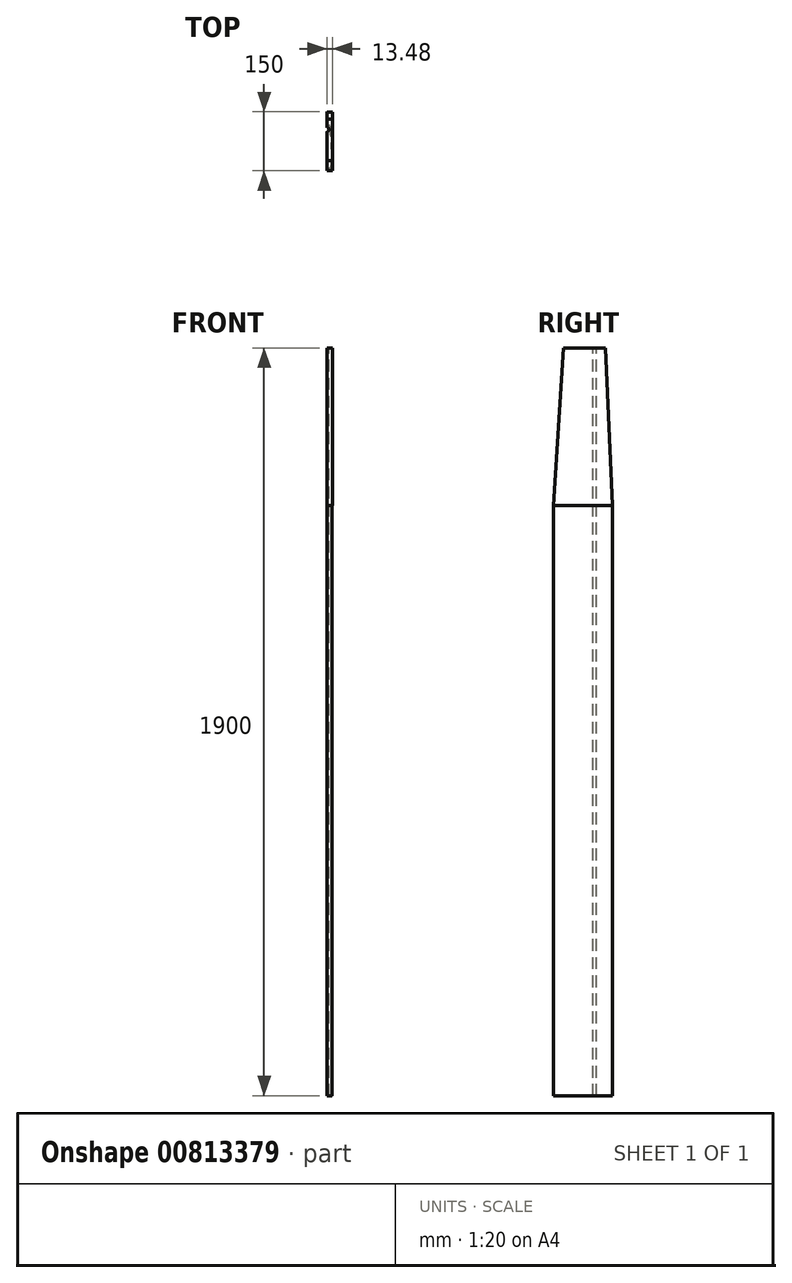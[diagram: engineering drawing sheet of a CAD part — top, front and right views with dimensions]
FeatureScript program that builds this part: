
annotation { "Feature Type Name" : "Feature", "Feature Type Description" : "" }
export const myFeature = defineFeature(function(context is Context, id is Id, definition is map)
    precondition{}
    {
        {
            var Q0;
            Q0=qCreatedBy(makeId("Top.planeOp"),FACE);
            var sketch = newSketch(context, id + "F0", { "sketchPlane" : qUnion([Q0])});
            skFitSpline(sketch, "E0", {"points": [v(0, 0) * mm, v(10.85, 19.16) * mm, v(11.95, 47.27) * mm, v(0, 150) * mm], "startDerivative": vector(86.36, 0) * mm, "endDerivative": vector(-49.91, 214.58) * mm});
            skLineSegment(sketch, "E1", {"start": v(0, 0) * mm, "end": v(0, 150) * mm});
            skSolve(sketch);
        }
        {
            var Q0;
            Q0=makeQuery(id+"F0.imprint","IMPRINT",FACE,{"disambiguationData":[TD([[makeQuery(id+"F0.imprint","IMPRINT",EDGE,{"derivedFrom":sQuery(id+"F0.wireOp",EDGE,"E0")}),1.0]])]});
            extrude(context, id + "F1", {"entities" : qUnion([Q0]), "oppositeDirection" : true, "depth" : 1500 * mm, "offsetDistance" : 25 * mm});
        }
        {
            var Q0;
            Q0=qCreatedBy(makeId("Top.planeOp"),FACE);
            var sketch = newSketch(context, id + "F2", { "sketchPlane" : qUnion([Q0])});
            skLineSegment(sketch, "E2.bottom", {"start": v(0, 0) * mm, "end": v(13.41, 0) * mm});
            skLineSegment(sketch, "E2.top", {"start": v(0, 149.72) * mm, "end": v(13.41, 149.72) * mm});
            skLineSegment(sketch, "E2.left", {"start": v(0, 0) * mm, "end": v(0, 149.72) * mm});
            skLineSegment(sketch, "E2.right", {"start": v(13.41, 0) * mm, "end": v(13.41, 149.72) * mm});
            skSolve(sketch);
        }
        {
            var Q0;
            Q0=qCreatedBy(makeId("Top.planeOp"),FACE);
            cPlane(context, id + "F3", {"entities" : qUnion([Q0]), "cplaneType" : CPlaneType.OFFSET, "offset" : 400 * mm, "width" : 150 * mm, "height" : 150 * mm});
        }
        {
            var Q0;
            Q0=qCreatedBy(id+"F3.planeOp",FACE);
            var sketch = newSketch(context, id + "F4", { "sketchPlane" : qUnion([Q0])});
            skLineSegment(sketch, "E3.bottom", {"start": v(0, 25.55) * mm, "end": v(13.48, 25.55) * mm});
            skLineSegment(sketch, "E3.top", {"start": v(0, 131.68) * mm, "end": v(13.48, 131.68) * mm});
            skLineSegment(sketch, "E3.left", {"start": v(0, 25.55) * mm, "end": v(0, 131.68) * mm});
            skLineSegment(sketch, "E3.right", {"start": v(13.48, 25.55) * mm, "end": v(13.48, 131.68) * mm});
            skSolve(sketch);
        }
        {
            var Q1;
            Q1=makeQuery(id+"F4.imprint","IMPRINT",FACE,{"disambiguationData":[TD([[makeQuery(id+"F4.imprint","IMPRINT",EDGE,{"derivedFrom":sQuery(id+"F4.wireOp",EDGE,"E3.bottom")}),1.0]])]});
            var Q2;
            Q2=makeQuery(id+"F2.imprint","IMPRINT",FACE,{"disambiguationData":[TD([[makeQuery(id+"F2.imprint","IMPRINT",EDGE,{"derivedFrom":sQuery(id+"F2.wireOp",EDGE,"E2.bottom")}),1.0]])]});
            loft(context, id + "F5", {"operationType" : NewBodyOperationType.ADD, "sheetProfilesArray" : [{ "sheetProfileEntities" : qUnion([Q1]) }, { "sheetProfileEntities" : qUnion([Q2]) }]});
        }
        {
            var Q0;
            Q0=qCreatedBy(id+"F3.planeOp",FACE);
            var sketch = newSketch(context, id + "F6", { "sketchPlane" : qUnion([Q0])});
            skArc(sketch, "E4", {"start": v(0, 100) * mm, "mid": v(5, 105) * mm, "end": v(0, 110) * mm});
            skLineSegment(sketch, "E5", {"start": v(0, 100) * mm, "end": v(0, 110) * mm});
            skSolve(sketch);
        }
        {
            var Q0;
            Q0=makeQuery(id+"F6.imprint","IMPRINT",FACE,{"disambiguationData":[TD([[makeQuery(id+"F6.imprint","IMPRINT",EDGE,{"derivedFrom":sQuery(id+"F6.wireOp",EDGE,"E4")}),1.0]])]});
            extrude(context, id + "F7", {"entities" : qUnion([Q0]), "operationType" : NewBodyOperationType.REMOVE, "endBound" : BoundingType.THROUGH_ALL, "oppositeDirection" : true, "depth" : 1900 * mm, "offsetDistance" : 25 * mm});
        }
    });
